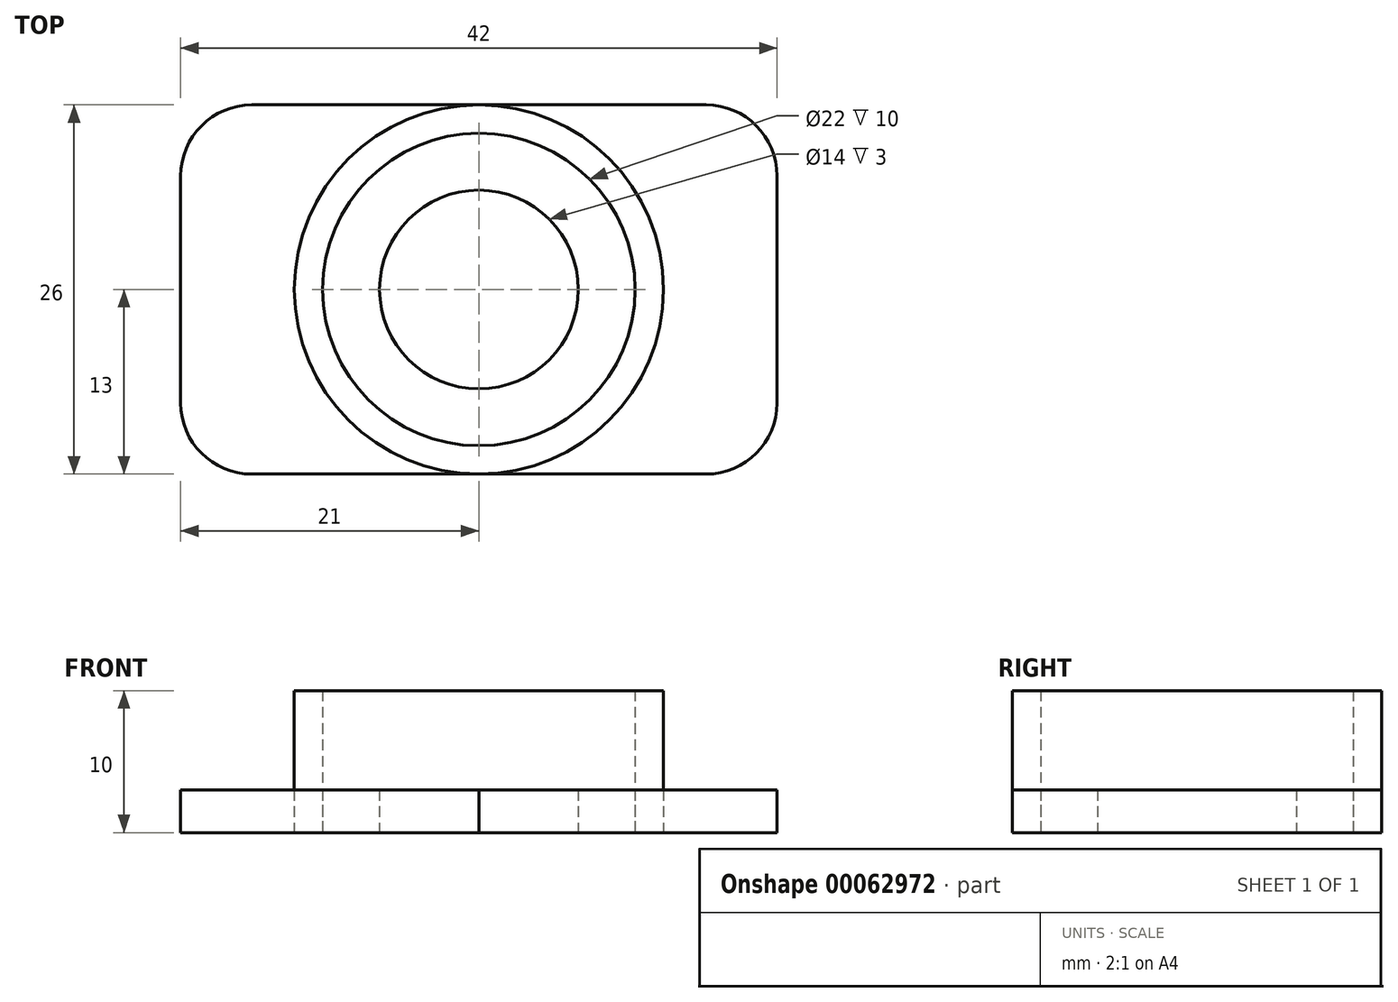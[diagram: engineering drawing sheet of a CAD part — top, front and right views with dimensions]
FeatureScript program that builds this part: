
annotation { "Feature Type Name" : "Feature", "Feature Type Description" : "" }
export const myFeature = defineFeature(function(context is Context, id is Id, definition is map)
    precondition{}
    {
        {
            var Q0;
            Q0=qCreatedBy(makeId("Top.planeOp"),FACE);
            var sketch = newSketch(context, id + "F0", { "sketchPlane" : qUnion([Q0])});
            skCircle(sketch, "E0", {"center": v(0, 0) * mm, "radius": 11 * mm});
            skCircle(sketch, "E1", {"center": v(0, 0) * mm, "radius": 4 * mm, "construction": true});
            skCircle(sketch, "E2.0", {"center": v(0, 0) * mm, "radius": 7 * mm});
            skLineSegment(sketch, "E3.rect.bottom", {"start": v(16, 13) * mm, "end": v(-16, 13) * mm});
            skLineSegment(sketch, "E3.rect.top", {"start": v(16, -13) * mm, "end": v(-16, -13) * mm});
            skLineSegment(sketch, "E3.rect.left", {"start": v(21, 8) * mm, "end": v(21, -8) * mm});
            skLineSegment(sketch, "E3.rect.right", {"start": v(-21, 8) * mm, "end": v(-21, -8) * mm});
            skCircle(sketch, "E4.0", {"center": v(0, 0) * mm, "radius": 13 * mm});
            skPoint(sketch, "E5.visualSharp", {"position": v(-21, 13) * mm});
            skArc(sketch, "E5.filletArc", {"start": v(-16, 13) * mm, "mid": v(-19.54, 11.54) * mm, "end": v(-21, 8) * mm});
            skPoint(sketch, "E6.visualSharp", {"position": v(-21, -13) * mm});
            skArc(sketch, "E6.filletArc", {"start": v(-21, -8) * mm, "mid": v(-19.54, -11.54) * mm, "end": v(-16, -13) * mm});
            skPoint(sketch, "E7.visualSharp", {"position": v(21, -13) * mm});
            skArc(sketch, "E7.filletArc", {"start": v(16, -13) * mm, "mid": v(19.54, -11.54) * mm, "end": v(21, -8) * mm});
            skPoint(sketch, "E8.visualSharp", {"position": v(21, 13) * mm});
            skArc(sketch, "E8.filletArc", {"start": v(21, 8) * mm, "mid": v(19.54, 11.54) * mm, "end": v(16, 13) * mm});
            skSolve(sketch);
        }
        {
            var Q0;
            Q0=makeQuery(id+"F0.imprint","IMPRINT",FACE,{"disambiguationData":[TD([[makeQuery(id+"F0.imprint","IMPRINT",EDGE,{"derivedFrom":sQuery(id+"F0.wireOp",EDGE,"E3.rect.bottom")}),1.0]])]});
            var Q1;
            Q1=makeQuery(id+"F0.imprint","IMPRINT",FACE,{"disambiguationData":[TD([[makeQuery(id+"F0.imprint","IMPRINT",EDGE,{"derivedFrom":sQuery(id+"F0.wireOp",EDGE,"E0")}),1.0]])]});
            extrude(context, id + "F1", {"entities" : qUnion([Q0, Q1]), "depth" : 3 * mm});
        }
        {
            var Q0;
            Q0=makeQuery(id+"F0.imprint","IMPRINT",FACE,{"disambiguationData":[TD([[makeQuery(id+"F0.imprint","IMPRINT",EDGE,{"derivedFrom":sQuery(id+"F0.wireOp",EDGE,"E0")}),-1.0]])]});
            extrude(context, id + "F2", {"entities" : qUnion([Q0]), "depth" : 10 * mm});
        }
    });
